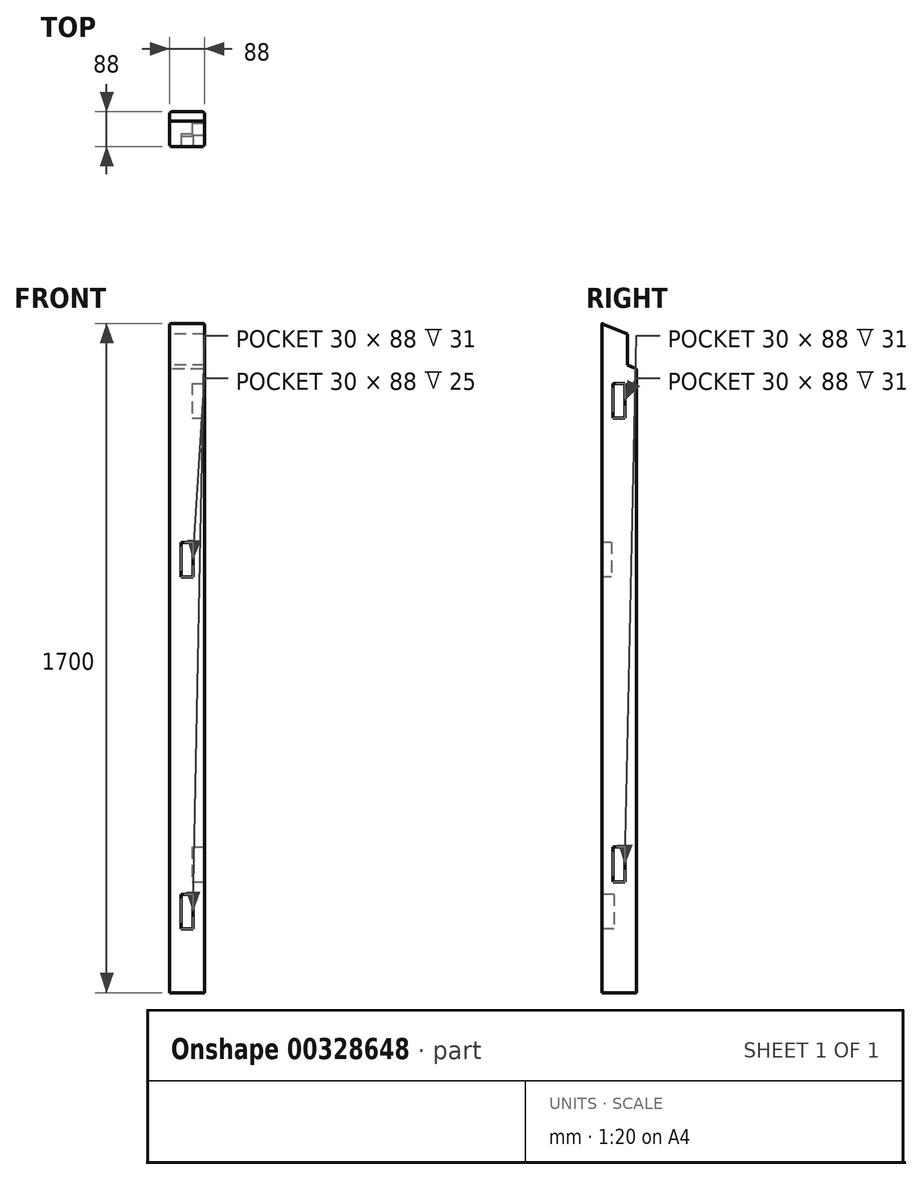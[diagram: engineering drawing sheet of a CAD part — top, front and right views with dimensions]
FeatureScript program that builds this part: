
annotation { "Feature Type Name" : "Feature", "Feature Type Description" : "" }
export const myFeature = defineFeature(function(context is Context, id is Id, definition is map)
    precondition{}
    {
        {
            var Q0;
            Q0=qCreatedBy(makeId("Top.planeOp"),FACE);
            var sketch = newSketch(context, id + "F0", { "sketchPlane" : qUnion([Q0])});
            skLineSegment(sketch, "E0.bottom", {"start": v(0, 0) * mm, "end": v(88, 0) * mm});
            skLineSegment(sketch, "E0.top", {"start": v(0, 88) * mm, "end": v(88, 88) * mm});
            skLineSegment(sketch, "E0.left", {"start": v(0, 0) * mm, "end": v(0, 88) * mm});
            skLineSegment(sketch, "E0.right", {"start": v(88, 0) * mm, "end": v(88, 88) * mm});
            skSolve(sketch);
        }
        {
            var Q0;
            Q0=qSketchRegion(id+"F0",true);
            extrude(context, id + "F1", {"entities" : qUnion([Q0]), "depth" : 1700 * mm});
        }
        {
            var Q0;
            Q0=makeQuery(id+"F1.opExtrude","SWEPT_FACE",FACE,{"disambiguationData":[OSD([sQuery(id+"F0.wireOp",EDGE,"E0.left")])]});
            var sketch = newSketch(context, id + "F2", { "sketchPlane" : qUnion([Q0])});
            skLineSegment(sketch, "E1", {"start": v(0, 1700) * mm, "end": v(-88, 1663.55) * mm});
            skLineSegment(sketch, "E2", {"start": v(-88, 1663.55) * mm, "end": v(-88, 1700) * mm});
            skLineSegment(sketch, "E3", {"start": v(-88, 1700) * mm, "end": v(0, 1700) * mm});
            skSolve(sketch);
        }
        {
            var Q0;
            Q0=qSketchRegion(id+"F2",true);
            extrude(context, id + "F3", {"entities" : qUnion([Q0]), "operationType" : NewBodyOperationType.REMOVE, "endBound" : BoundingType.THROUGH_ALL, "oppositeDirection" : true, "depth" : 351.8 * mm});
        }
        {
            var Q0;
            Q0=makeQuery(id+"F1.opExtrude","SWEPT_FACE",FACE,{"disambiguationData":[OSD([sQuery(id+"F0.wireOp",EDGE,"E0.left")])]});
            var sketch = newSketch(context, id + "F4", { "sketchPlane" : qUnion([Q0])});
            skLineSegment(sketch, "E4", {"start": v(-65, 1673.08) * mm, "end": v(-65, 1594.08) * mm});
            skLineSegment(sketch, "E5", {"start": v(-88, 1663.55) * mm, "end": v(-65, 1673.08) * mm});
            skLineSegment(sketch, "E6", {"start": v(-65, 1594.08) * mm, "end": v(-88, 1584.55) * mm});
            skLineSegment(sketch, "E7", {"start": v(-88, 1663.55) * mm, "end": v(-88, 1584.55) * mm});
            skSolve(sketch);
        }
        {
            var Q0;
            Q0=qSketchRegion(id+"F4",true);
            extrude(context, id + "F5", {"entities" : qUnion([Q0]), "operationType" : NewBodyOperationType.REMOVE, "endBound" : BoundingType.THROUGH_ALL, "oppositeDirection" : true, "depth" : 529.35 * mm});
        }
        {
            var Q0;
            Q0=makeQuery(id+"F1.opExtrude","SWEPT_FACE",FACE,{"disambiguationData":[OSD([sQuery(id+"F0.wireOp",EDGE,"E0.right")])]});
            var sketch = newSketch(context, id + "F6", { "sketchPlane" : qUnion([Q0])});
            skLineSegment(sketch, "E8", {"start": v(44, 0) * mm, "end": v(44, 282) * mm, "construction": true});
            skPoint(sketch, "E8.endSnap0", {"position": v(44, 0) * mm});
            skLineSegment(sketch, "E9", {"start": v(44, 282) * mm, "end": v(29, 282) * mm});
            skLineSegment(sketch, "E10", {"start": v(29, 282) * mm, "end": v(29, 370) * mm});
            skLineSegment(sketch, "E11", {"start": v(29, 370) * mm, "end": v(59, 370) * mm});
            skLineSegment(sketch, "E12", {"start": v(59, 370) * mm, "end": v(59, 282) * mm});
            skLineSegment(sketch, "E13", {"start": v(59, 282) * mm, "end": v(44, 282) * mm});
            skSolve(sketch);
        }
        {
            var Q0;
            Q0=qSketchRegion(id+"F6",true);
            extrude(context, id + "F7", {"entities" : qUnion([Q0]), "operationType" : NewBodyOperationType.REMOVE, "oppositeDirection" : true, "depth" : 31 * mm});
        }
        {
            var Q0;
            Q0=makeQuery(id+"F1.opExtrude","SWEPT_FACE",FACE,{"disambiguationData":[OSD([sQuery(id+"F0.wireOp",EDGE,"E0.right")])]});
            var sketch = newSketch(context, id + "F8", { "sketchPlane" : qUnion([Q0])});
            skLineSegment(sketch, "E14", {"start": v(44, 0) * mm, "end": v(44, 1460) * mm, "construction": true});
            skPoint(sketch, "E14.endSnap0", {"position": v(44, 370) * mm});
            skLineSegment(sketch, "E15", {"start": v(44, 1460) * mm, "end": v(29, 1460) * mm});
            skLineSegment(sketch, "E16", {"start": v(29, 1460) * mm, "end": v(29, 1548) * mm});
            skLineSegment(sketch, "E17", {"start": v(29, 1548) * mm, "end": v(59, 1548) * mm});
            skLineSegment(sketch, "E18", {"start": v(59, 1548) * mm, "end": v(59, 1460) * mm});
            skLineSegment(sketch, "E19", {"start": v(59, 1460) * mm, "end": v(44, 1460) * mm});
            skSolve(sketch);
        }
        {
            var Q0;
            Q0=qSketchRegion(id+"F8",true);
            extrude(context, id + "F9", {"entities" : qUnion([Q0]), "operationType" : NewBodyOperationType.REMOVE, "oppositeDirection" : true, "depth" : 31 * mm});
        }
        {
            var Q0;
            Q0=makeQuery(id+"F1.opExtrude","SWEPT_FACE",FACE,{"disambiguationData":[OSD([sQuery(id+"F0.wireOp",EDGE,"E0.bottom")])]});
            var sketch = newSketch(context, id + "F10", { "sketchPlane" : qUnion([Q0])});
            skLineSegment(sketch, "E20", {"start": v(44, 0) * mm, "end": v(44, 162) * mm, "construction": true});
            skLineSegment(sketch, "E21", {"start": v(44, 162) * mm, "end": v(29, 162) * mm});
            skLineSegment(sketch, "E22", {"start": v(29, 162) * mm, "end": v(29, 250) * mm});
            skLineSegment(sketch, "E23", {"start": v(29, 250) * mm, "end": v(59, 250) * mm});
            skLineSegment(sketch, "E24", {"start": v(59, 250) * mm, "end": v(59, 162) * mm});
            skLineSegment(sketch, "E25", {"start": v(59, 162) * mm, "end": v(44, 162) * mm});
            skSolve(sketch);
        }
        {
            var Q0;
            Q0=qSketchRegion(id+"F10",true);
            extrude(context, id + "F11", {"entities" : qUnion([Q0]), "operationType" : NewBodyOperationType.REMOVE, "oppositeDirection" : true, "depth" : 31 * mm});
        }
        {
            var Q0;
            Q0=makeQuery(id+"F1.opExtrude","SWEPT_FACE",FACE,{"disambiguationData":[OSD([sQuery(id+"F0.wireOp",EDGE,"E0.bottom")])]});
            var sketch = newSketch(context, id + "F12", { "sketchPlane" : qUnion([Q0])});
            skLineSegment(sketch, "E26", {"start": v(44, 0) * mm, "end": v(44, 1056) * mm, "construction": true});
            skLineSegment(sketch, "E27", {"start": v(44, 1056) * mm, "end": v(29, 1056) * mm});
            skLineSegment(sketch, "E28", {"start": v(29, 1056) * mm, "end": v(29, 1144) * mm});
            skLineSegment(sketch, "E29", {"start": v(29, 1144) * mm, "end": v(59, 1144) * mm});
            skLineSegment(sketch, "E30", {"start": v(59, 1144) * mm, "end": v(59, 1056) * mm});
            skLineSegment(sketch, "E31", {"start": v(59, 1056) * mm, "end": v(44, 1056) * mm});
            skSolve(sketch);
        }
        {
            var Q0;
            Q0=qSketchRegion(id+"F12",true);
            extrude(context, id + "F13", {"entities" : qUnion([Q0]), "operationType" : NewBodyOperationType.REMOVE, "oppositeDirection" : true, "depth" : 25 * mm});
        }
        {
            var Q0;
            Q0=makeQuery(id+"F1.opExtrude","SWEPT_EDGE",EDGE,{"disambiguationData":[OSD([sQuery(id+"F0.wireOp",EDGE,"E0.bottom"),sQuery(id+"F0.wireOp",EDGE,"E0.right")])]});
            var Q1;
            Q1=makeQuery(id+"F1.opExtrude","SWEPT_EDGE",EDGE,{"disambiguationData":[OSD([sQuery(id+"F0.wireOp",EDGE,"E0.bottom"),sQuery(id+"F0.wireOp",EDGE,"E0.left")])]});
            var Q2;
            Q2=makeQuery(id+"F1.opExtrude","SWEPT_EDGE",EDGE,{"disambiguationData":[OSD([sQuery(id+"F0.wireOp",EDGE,"E0.top"),sQuery(id+"F0.wireOp",EDGE,"E0.right")])]});
            var Q3;
            Q3=makeQuery(id+"F1.opExtrude","SWEPT_EDGE",EDGE,{"disambiguationData":[OSD([sQuery(id+"F0.wireOp",EDGE,"E0.top"),sQuery(id+"F0.wireOp",EDGE,"E0.left")])]});
            fillet(context, id + "F14", {"entities" : qUnion([Q0, Q1, Q2, Q3]), "radius" : 5 * mm, "tangentPropagation" : true, "allowEdgeOverflow" : false});
        }
    });
